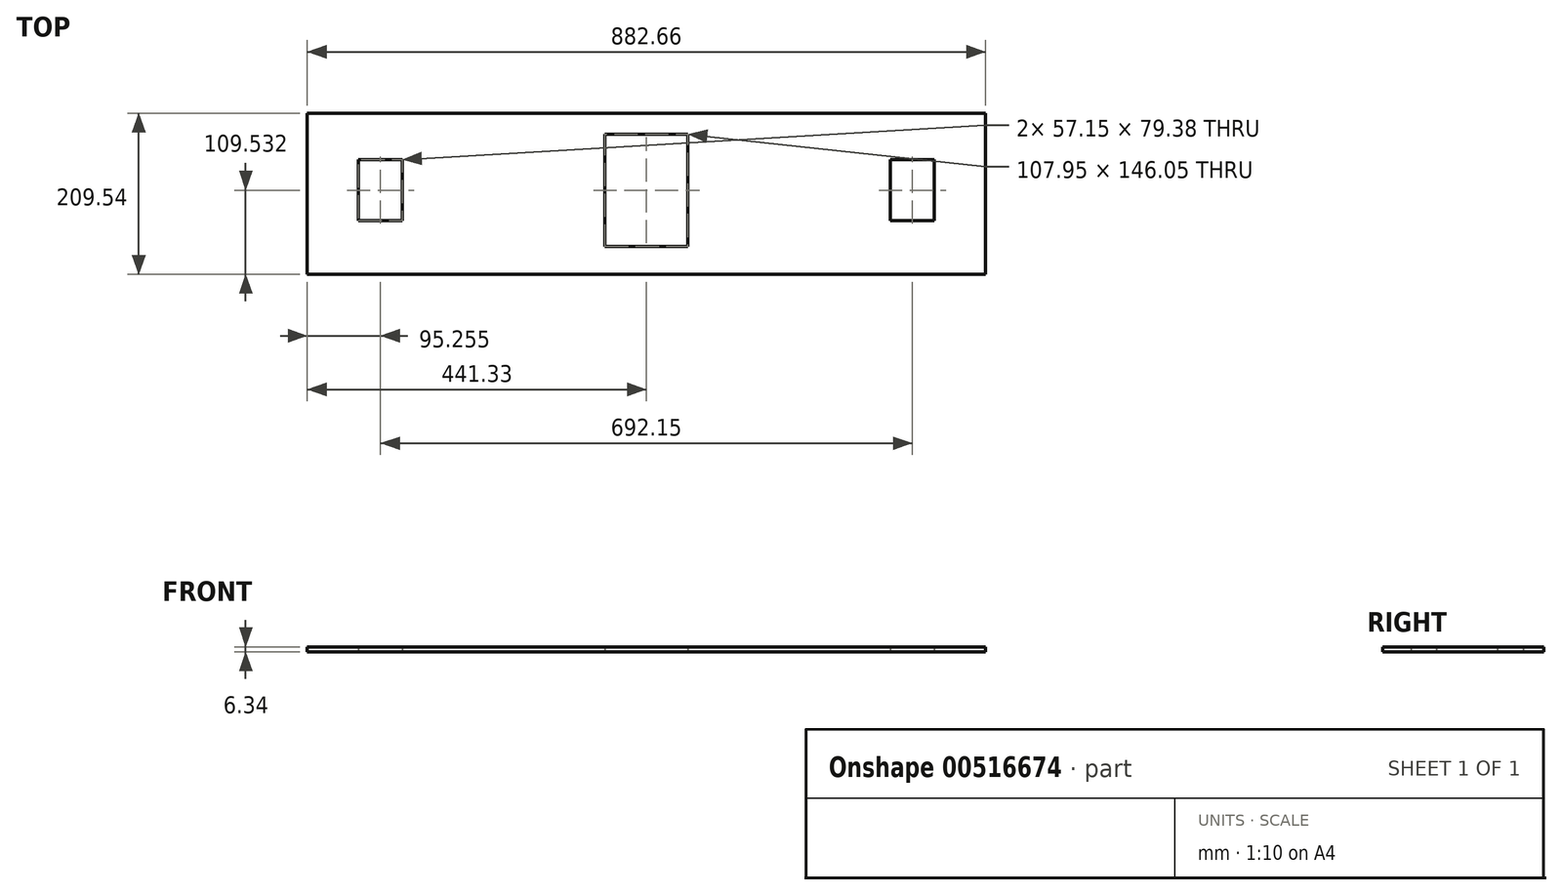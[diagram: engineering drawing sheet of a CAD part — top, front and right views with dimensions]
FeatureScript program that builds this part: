
annotation { "Feature Type Name" : "Feature", "Feature Type Description" : "" }
export const myFeature = defineFeature(function(context is Context, id is Id, definition is map)
    precondition{}
    {
        {
            var Q0;
            Q0=qCreatedBy(makeId("Top.planeOp"),FACE);
            var sketch = newSketch(context, id + "F0", { "sketchPlane" : qUnion([Q0])});
            skLineSegment(sketch, "E0.bottom", {"start": v(441.33, 104.78) * mm, "end": v(-441.33, 104.77) * mm});
            skLineSegment(sketch, "E0.top", {"start": v(441.33, -104.77) * mm, "end": v(-441.33, -104.78) * mm});
            skLineSegment(sketch, "E0.left", {"start": v(441.32, 104.78) * mm, "end": v(441.33, -104.77) * mm});
            skLineSegment(sketch, "E0.right", {"start": v(-441.33, 104.77) * mm, "end": v(-441.32, -104.78) * mm});
            skPoint(sketch, "E0.middle", {"position": v(0, 0) * mm});
            skLineSegment(sketch, "E1.bottom", {"start": v(-317.5, 44.45) * mm, "end": v(-374.65, 44.45) * mm});
            skLineSegment(sketch, "E1.top", {"start": v(-317.5, -34.93) * mm, "end": v(-374.65, -34.93) * mm});
            skLineSegment(sketch, "E1.left", {"start": v(-317.5, 44.45) * mm, "end": v(-317.5, -34.93) * mm});
            skLineSegment(sketch, "E1.right", {"start": v(-374.65, 44.45) * mm, "end": v(-374.65, -34.93) * mm});
            skPoint(sketch, "E1.middle", {"position": v(-346.08, 4.76) * mm});
            skLineSegment(sketch, "E2.bottom", {"start": v(53.98, 77.79) * mm, "end": v(-53.98, 77.79) * mm});
            skLineSegment(sketch, "E2.top", {"start": v(53.98, -68.26) * mm, "end": v(-53.97, -68.26) * mm});
            skLineSegment(sketch, "E2.left", {"start": v(53.97, 77.79) * mm, "end": v(53.98, -68.26) * mm});
            skLineSegment(sketch, "E2.right", {"start": v(-53.98, 77.79) * mm, "end": v(-53.98, -68.26) * mm});
            skPoint(sketch, "E2.middle", {"position": v(0, 4.76) * mm});
            skLineSegment(sketch, "E3.bottom", {"start": v(374.65, 44.45) * mm, "end": v(317.5, 44.45) * mm});
            skLineSegment(sketch, "E3.top", {"start": v(374.65, -34.93) * mm, "end": v(317.5, -34.93) * mm});
            skLineSegment(sketch, "E3.left", {"start": v(374.65, 44.45) * mm, "end": v(374.65, -34.93) * mm});
            skLineSegment(sketch, "E3.right", {"start": v(317.5, 44.45) * mm, "end": v(317.5, -34.93) * mm});
            skPoint(sketch, "E3.middle", {"position": v(346.08, 4.76) * mm});
            skSolve(sketch);
        }
        {
            var Q0;
            Q0=makeQuery(id+"F0.imprint","IMPRINT",FACE,{"disambiguationData":[TD([[makeQuery(id+"F0.imprint","IMPRINT",EDGE,{"derivedFrom":sQuery(id+"F0.wireOp",EDGE,"E0.bottom")}),1.0]])]});
            extrude(context, id + "F1", {"entities" : qUnion([Q0]), "endBound" : BoundingType.SYMMETRIC, "depth" : 6.35 * mm, "offsetDistance" : 25.4 * mm});
        }
    });
